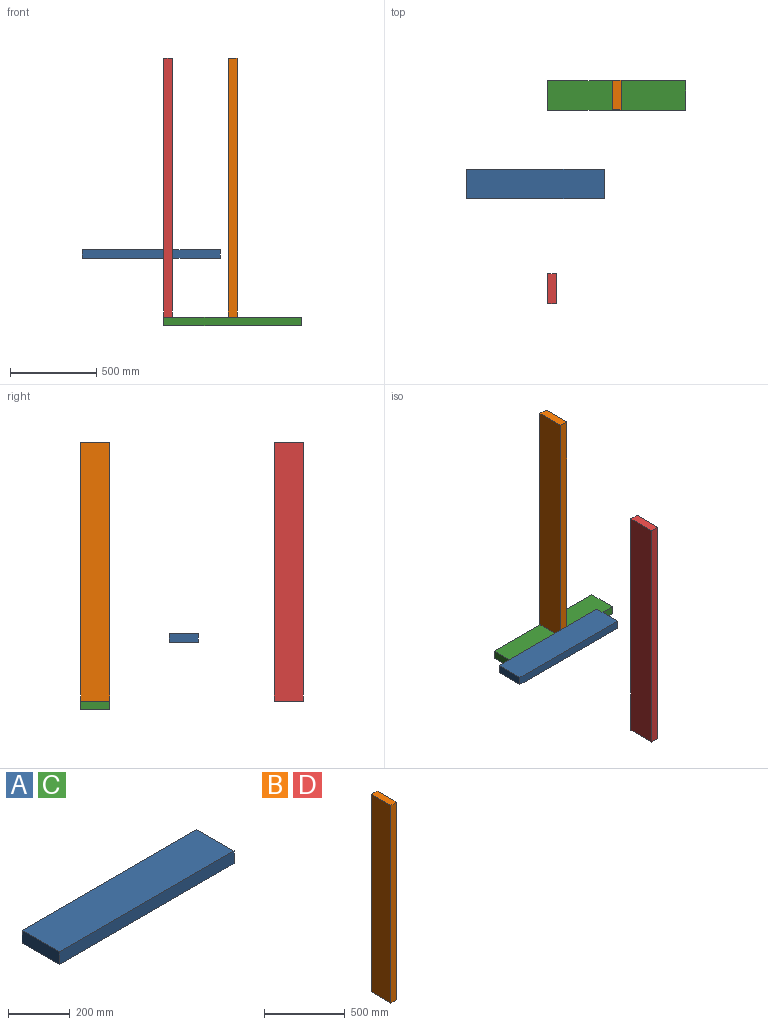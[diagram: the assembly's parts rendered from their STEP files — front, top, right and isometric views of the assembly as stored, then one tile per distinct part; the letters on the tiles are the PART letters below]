
ASSEMBLY  parts=4 mates=3
PART A: 6 faces, bbox 800x170x50 mm
  f0: plane 800x50mm, normal (0,1,0), area 40000mm2, adj f1,f3,f4,f5
  f1: plane 170x50mm, normal (-1,0,0), area 8500mm2, adj f0,f2,f4,f5
  f2: plane 800x50mm, normal (0,-1,0), area 40000mm2, adj f1,f3,f4,f5
  f3: plane 170x50mm, normal (1,0,0), area 8500mm2, adj f0,f2,f4,f5
  f4: plane 800x170mm, normal (0,0,1), area 136000mm2, adj f0,f1,f2,f3
  f5: plane 800x170mm, normal (0,0,-1), area 136000mm2, adj f0,f1,f2,f3
PART B: 6 faces, bbox 50x170x1500 mm
  f0: plane 1500x50mm, normal (0,1,0), area 75000mm2, adj f1,f3,f4,f5
  f1: plane 1500x170mm, normal (-1,0,0), area 255000mm2, adj f0,f2,f4,f5
  f2: plane 1500x50mm, normal (0,-1,0), area 75000mm2, adj f1,f3,f4,f5
  f3: plane 1500x170mm, normal (1,0,0), area 255000mm2, adj f0,f2,f4,f5
  f4: plane 170x50mm, normal (0,0,1), area 8500mm2, adj f0,f1,f2,f3
  f5: plane 170x50mm, normal (0,0,-1), area 8500mm2, adj f0,f1,f2,f3
PART C: same geometry as A
PART D: same geometry as B
PLACE A t=(915.23,608.05,119.46)mm
PLACE B t=(1807.93,896.47,-221)mm
PLACE C t=(1387.19,1121.21,-271)mm
PLACE D t=(1432.93,-224.74,-221)mm
MATE planar C.f4 <-> B.f5  axis (0,0,1) through (1385.25,949.94,-221)mm
MATE planar D.f5 <-> C.f4  axis (0,0,-1) through (1010.25,-171.27,-221)mm
MATE planar D.f1 <-> C.f1  axis (-1,0,0) through (985.25,-171.27,529)mm
